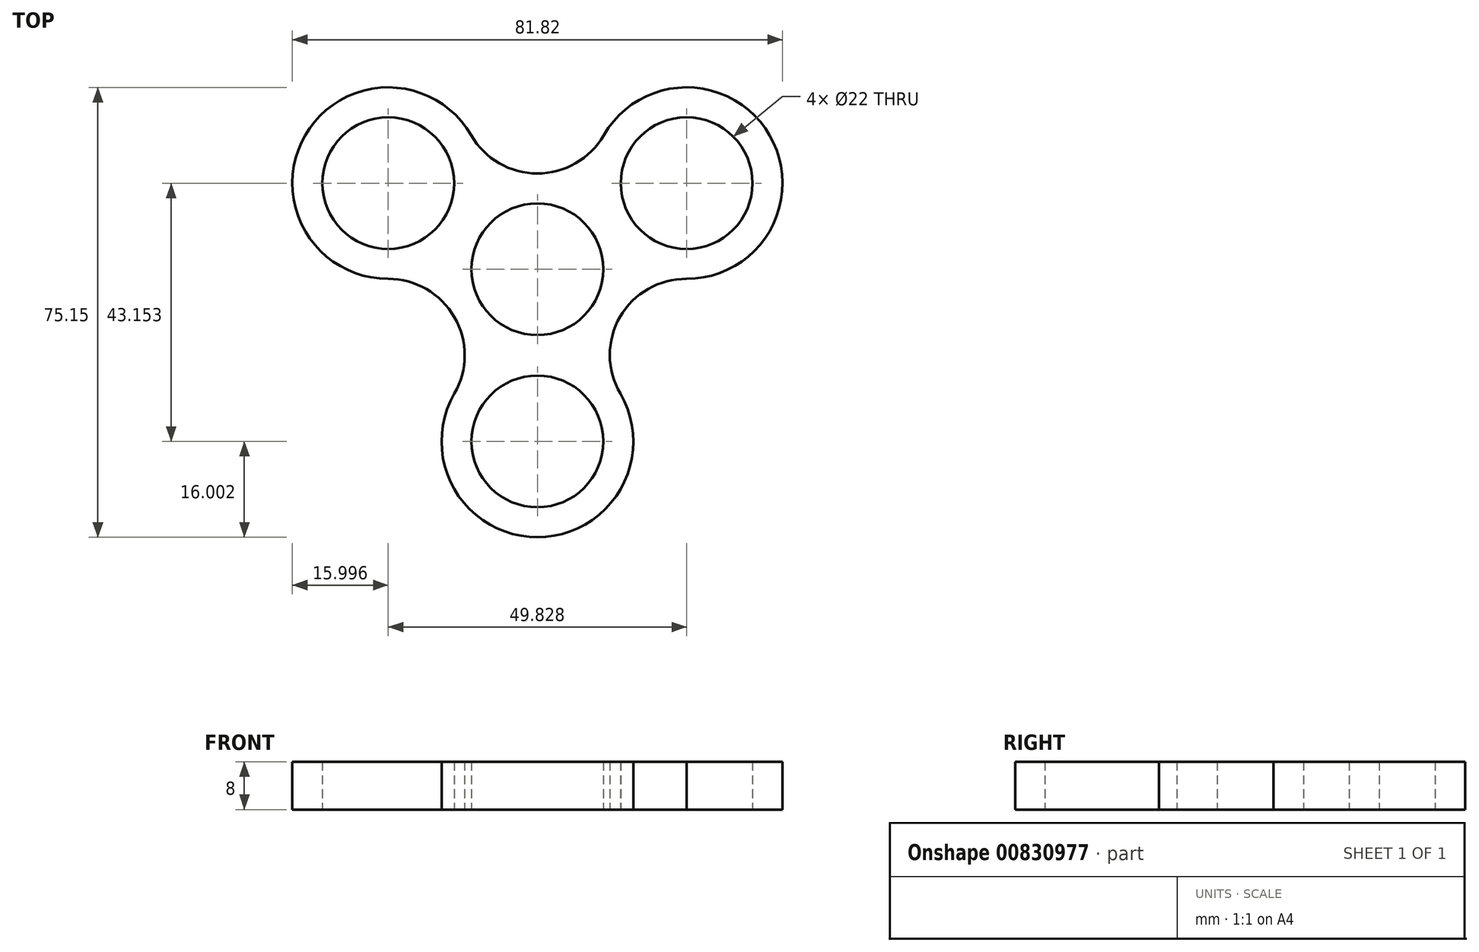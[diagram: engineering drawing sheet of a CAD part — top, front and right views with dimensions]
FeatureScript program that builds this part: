
annotation { "Feature Type Name" : "Feature", "Feature Type Description" : "" }
export const myFeature = defineFeature(function(context is Context, id is Id, definition is map)
    precondition{}
    {
        {
            var Q0;
            Q0=qCreatedBy(makeId("Top.planeOp"),FACE);
            var sketch = newSketch(context, id + "F0", { "sketchPlane" : qUnion([Q0])});
            skLineSegment(sketch, "E0", {"start": v(0, 0) * mm, "end": v(0, -28.77) * mm});
            skLineSegment(sketch, "E1", {"start": v(0, 0) * mm, "end": v(24.91, 14.38) * mm});
            skLineSegment(sketch, "E2", {"start": v(0, 0) * mm, "end": v(-24.91, 14.38) * mm});
            skArc(sketch, "E3", {"start": v(11.06, 22.38) * mm, "mid": v(38.77, 22.38) * mm, "end": v(24.91, -1.62) * mm});
            skArc(sketch, "E4", {"start": v(-11.06, 22.38) * mm, "mid": v(-38.77, 22.38) * mm, "end": v(-24.91, -1.62) * mm});
            skArc(sketch, "E5", {"start": v(-13.86, -20.77) * mm, "mid": v(0, -44.77) * mm, "end": v(13.86, -20.77) * mm});
            skCircle(sketch, "E6", {"center": v(0, 0) * mm, "radius": 11 * mm});
            skCircle(sketch, "E7", {"center": v(-24.91, 14.38) * mm, "radius": 11 * mm});
            skCircle(sketch, "E8", {"center": v(24.91, 14.38) * mm, "radius": 11 * mm});
            skCircle(sketch, "E9", {"center": v(0, -28.77) * mm, "radius": 11 * mm});
            skLineSegment(sketch, "E10", {"start": v(-24.91, 14.38) * mm, "end": v(53.21, -30.72) * mm, "construction": true});
            skLineSegment(sketch, "E11", {"start": v(24.91, 14.38) * mm, "end": v(-55.51, -32.05) * mm, "construction": true});
            skLineSegment(sketch, "E12", {"start": v(0, -28.77) * mm, "end": v(0, 35.37) * mm, "construction": true});
            skLineSegment(sketch, "E13", {"start": v(0, 41.54) * mm, "end": v(-35.97, -20.77) * mm, "construction": true});
            skLineSegment(sketch, "E14", {"start": v(-35.97, -20.77) * mm, "end": v(35.97, -20.77) * mm, "construction": true});
            skLineSegment(sketch, "E15", {"start": v(35.97, -20.77) * mm, "end": v(0, 41.54) * mm, "construction": true});
            skArc(sketch, "E16", {"start": v(-13.86, -20.77) * mm, "mid": v(-13.86, -8) * mm, "end": v(-24.91, -1.62) * mm});
            skArc(sketch, "E17", {"start": v(24.91, -1.62) * mm, "mid": v(13.79, -7.96) * mm, "end": v(13.86, -20.77) * mm});
            skArc(sketch, "E18", {"start": v(-11.06, 22.38) * mm, "mid": v(0, 16) * mm, "end": v(11.06, 22.38) * mm});
            skSolve(sketch);
        }
        {
            var Q0;
            Q0 = qSketchRegion(id + "F0", true);
            extrude(context, id + "F1", {"entities" : qUnion([Q0]), "depth" : 8 * mm, "offsetDistance" : 25 * mm});
        }
    });
